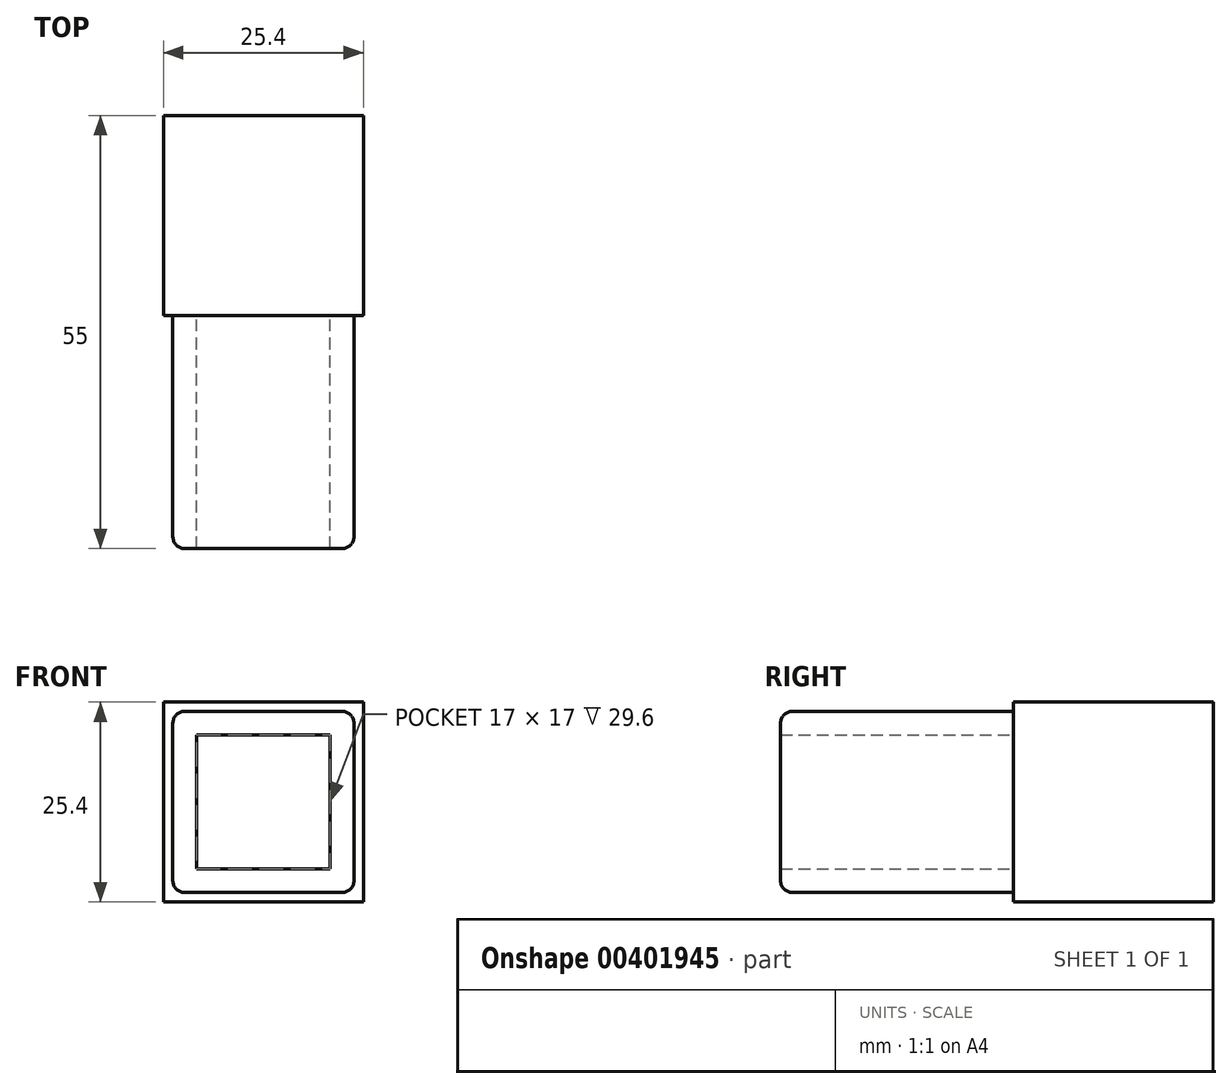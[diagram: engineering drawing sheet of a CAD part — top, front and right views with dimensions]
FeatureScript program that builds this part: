
annotation { "Feature Type Name" : "Feature", "Feature Type Description" : "" }
export const myFeature = defineFeature(function(context is Context, id is Id, definition is map)
    precondition{}
    {
        {
            var Q0;
            Q0=qCreatedBy(makeId("Front.planeOp"),FACE);
            var sketch = newSketch(context, id + "F0", { "sketchPlane" : qUnion([Q0])});
            skLineSegment(sketch, "E0.bottom", {"start": v(-12.7, 12.7) * mm, "end": v(12.7, 12.7) * mm});
            skLineSegment(sketch, "E0.top", {"start": v(-12.7, -12.7) * mm, "end": v(12.7, -12.7) * mm});
            skLineSegment(sketch, "E0.left", {"start": v(-12.7, 12.7) * mm, "end": v(-12.7, -12.7) * mm});
            skLineSegment(sketch, "E0.right", {"start": v(12.7, 12.7) * mm, "end": v(12.7, -12.7) * mm});
            skLineSegment(sketch, "E1", {"start": v(-12.7, 0) * mm, "end": v(0, 0) * mm, "construction": true});
            skLineSegment(sketch, "E2", {"start": v(0, 0) * mm, "end": v(0, 12.7) * mm, "construction": true});
            skSolve(sketch);
        }
        {
            var Q0;
            Q0=makeQuery(id+"F0.imprint","IMPRINT",FACE,{"disambiguationData":[TD([[makeQuery(id+"F0.imprint","IMPRINT",EDGE,{"derivedFrom":sQuery(id+"F0.wireOp",EDGE,"E0.bottom")}),-1.0]])]});
            extrude(context, id + "F1", {"entities" : qUnion([Q0]), "endBound" : BoundingType.SYMMETRIC, "depth" : 25.4 * mm});
        }
        {
            var Q0;
            Q0=makeQuery(id+"F1.opExtrude","CAP_FACE",FACE,{"disambiguationData":[OSD([sQuery(id+"F0.wireOp",EDGE,"E0.bottom"),sQuery(id+"F0.wireOp",EDGE,"E0.top"),sQuery(id+"F0.wireOp",EDGE,"E0.left"),sQuery(id+"F0.wireOp",EDGE,"E0.right")])],"isStart":false});
            var sketch = newSketch(context, id + "F2", { "sketchPlane" : qUnion([Q0])});
            skLineSegment(sketch, "E3.0", {"start": v(-11.5, 11.5) * mm, "end": v(-11.5, -11.5) * mm});
            skLineSegment(sketch, "E3.1", {"start": v(11.5, 11.5) * mm, "end": v(-11.5, 11.5) * mm});
            skLineSegment(sketch, "E3.2", {"start": v(11.5, -11.5) * mm, "end": v(11.5, 11.5) * mm});
            skLineSegment(sketch, "E3.3", {"start": v(-11.5, -11.5) * mm, "end": v(11.5, -11.5) * mm});
            skLineSegment(sketch, "E4.0.1", {"start": v(-12.7, -12.7) * mm, "end": v(12.7, -12.7) * mm});
            skLineSegment(sketch, "E5.0", {"start": v(8.5, 8.5) * mm, "end": v(-8.5, 8.5) * mm});
            skLineSegment(sketch, "E5.1", {"start": v(8.5, -8.5) * mm, "end": v(8.5, 8.5) * mm});
            skLineSegment(sketch, "E5.2", {"start": v(-8.5, -8.5) * mm, "end": v(8.5, -8.5) * mm});
            skLineSegment(sketch, "E5.3", {"start": v(-8.5, 8.5) * mm, "end": v(-8.5, -8.5) * mm});
            skSolve(sketch);
        }
        {
            var Q0;
            Q0 = qSketchRegion(id + "F2", true);
            extrude(context, id + "F3", {"entities" : qUnion([Q0]), "operationType" : NewBodyOperationType.ADD, "depth" : (55 - 25.4) * mm});
        }
        {
            var Q0;
            Q0=makeQuery(id+"F3.opExtrude","SWEPT_EDGE",EDGE,{"disambiguationData":[OSD([sQuery(id+"F2.wireOp",EDGE,"E3.1"),sQuery(id+"F2.wireOp",EDGE,"E3.2")])]});
            var Q1;
            Q1=makeQuery(id+"F3.opExtrude","SWEPT_EDGE",EDGE,{"disambiguationData":[OSD([sQuery(id+"F2.wireOp",EDGE,"E3.2"),sQuery(id+"F2.wireOp",EDGE,"E3.3")])]});
            var Q2;
            Q2=makeQuery(id+"F3.opExtrude","SWEPT_EDGE",EDGE,{"disambiguationData":[OSD([sQuery(id+"F2.wireOp",EDGE,"E3.0"),sQuery(id+"F2.wireOp",EDGE,"E3.1")])]});
            var Q3;
            Q3=makeQuery(id+"F3.opExtrude","SWEPT_EDGE",EDGE,{"disambiguationData":[OSD([sQuery(id+"F2.wireOp",EDGE,"E3.0"),sQuery(id+"F2.wireOp",EDGE,"E3.3")])]});
            var Q4;
            Q4=makeQuery(id+"F3.opExtrude","CAP_EDGE",EDGE,{"disambiguationData":[OSD([sQuery(id+"F2.wireOp",EDGE,"E3.1")])],"isStart":false});
            var Q5;
            Q5=makeQuery(id+"F3.opExtrude","CAP_EDGE",EDGE,{"disambiguationData":[OSD([sQuery(id+"F2.wireOp",EDGE,"E3.2")])],"isStart":false});
            var Q6;
            Q6=makeQuery(id+"F3.opExtrude","CAP_EDGE",EDGE,{"disambiguationData":[OSD([sQuery(id+"F2.wireOp",EDGE,"E3.3")])],"isStart":false});
            var Q7;
            Q7=makeQuery(id+"F3.opExtrude","CAP_EDGE",EDGE,{"disambiguationData":[OSD([sQuery(id+"F2.wireOp",EDGE,"E3.0")])],"isStart":false});
            fillet(context, id + "F4", {"entities" : qUnion([Q0, Q1, Q2, Q3, Q4, Q5, Q6, Q7]), "radius" : 1.5 * mm, "tangentPropagation" : true, "allowEdgeOverflow" : false});
        }
        {
            var Q0;
            Q0=qCreatedBy(makeId("Front.planeOp"),FACE);
            var sketch = newSketch(context, id + "F5", { "sketchPlane" : qUnion([Q0])});
            skLineSegment(sketch, "E6", {"start": v(0, 70.28) * mm, "end": v(0, -12.35) * mm, "construction": true});
            skSolve(sketch);
        }
    });
